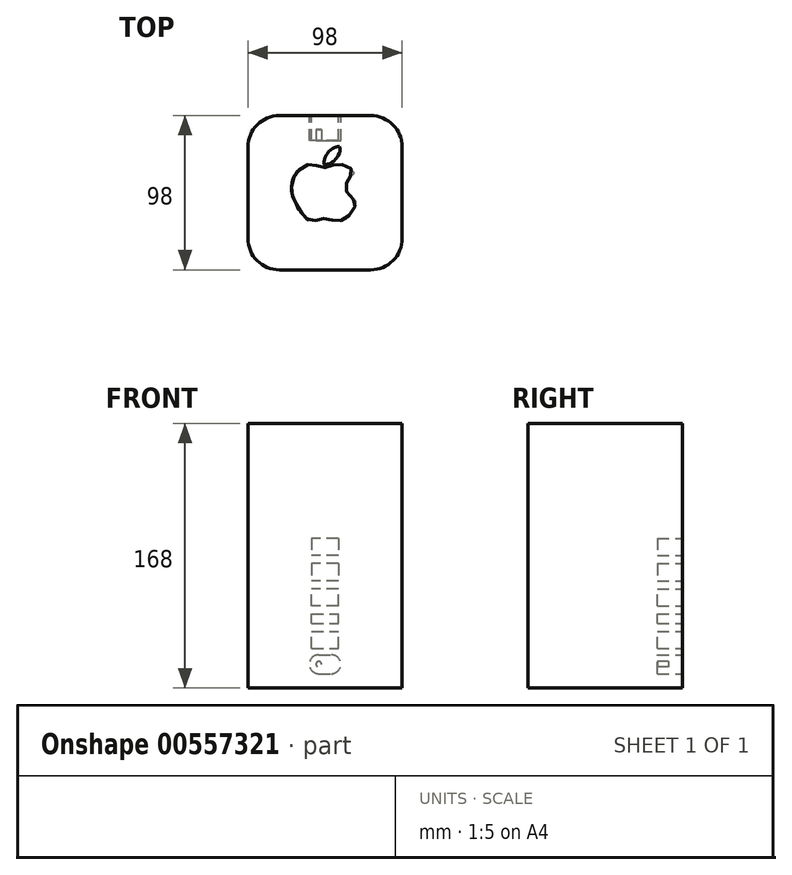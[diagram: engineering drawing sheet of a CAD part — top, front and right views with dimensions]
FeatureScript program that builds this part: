
annotation { "Feature Type Name" : "Feature", "Feature Type Description" : "" }
export const myFeature = defineFeature(function(context is Context, id is Id, definition is map)
    precondition{}
    {
        {
            var Q0;
            Q0=qCreatedBy(makeId("Top.planeOp"),FACE);
            var sketch = newSketch(context, id + "F0", { "sketchPlane" : qUnion([Q0])});
            skLineSegment(sketch, "E0.bottom", {"start": v(-49, 49) * mm, "end": v(49, 49) * mm});
            skLineSegment(sketch, "E0.top", {"start": v(-49, -49) * mm, "end": v(49, -49) * mm});
            skLineSegment(sketch, "E0.left", {"start": v(-49, 49) * mm, "end": v(-49, -49) * mm});
            skLineSegment(sketch, "E0.right", {"start": v(49, 49) * mm, "end": v(49, -49) * mm});
            skPoint(sketch, "E0.middle", {"position": v(0, 0) * mm});
            skSolve(sketch);
        }
        {
            var Q0;
            Q0=makeQuery(id+"F0.imprint","IMPRINT",FACE,{"disambiguationData":[TD([[makeQuery(id+"F0.imprint","IMPRINT",EDGE,{"derivedFrom":sQuery(id+"F0.wireOp",EDGE,"E0.bottom")}),-1.0]])]});
            extrude(context, id + "F1", {"entities" : qUnion([Q0]), "depth" : 168 * mm, "offsetDistance" : 25 * mm});
        }
        {
            var Q0;
            Q0=makeQuery(id+"F1.opExtrude","SWEPT_EDGE",EDGE,{"disambiguationData":[OSD([sQuery(id+"F0.wireOp",EDGE,"E0.top"),sQuery(id+"F0.wireOp",EDGE,"E0.left")])]});
            var Q1;
            Q1=makeQuery(id+"F1.opExtrude","SWEPT_EDGE",EDGE,{"disambiguationData":[OSD([sQuery(id+"F0.wireOp",EDGE,"E0.top"),sQuery(id+"F0.wireOp",EDGE,"E0.right")])]});
            var Q2;
            Q2=makeQuery(id+"F1.opExtrude","SWEPT_EDGE",EDGE,{"disambiguationData":[OSD([sQuery(id+"F0.wireOp",EDGE,"E0.bottom"),sQuery(id+"F0.wireOp",EDGE,"E0.right")])]});
            var Q3;
            Q3=makeQuery(id+"F1.opExtrude","SWEPT_EDGE",EDGE,{"disambiguationData":[OSD([sQuery(id+"F0.wireOp",EDGE,"E0.bottom"),sQuery(id+"F0.wireOp",EDGE,"E0.left")])]});
            fillet(context, id + "F2", {"entities" : qUnion([Q0, Q1, Q2, Q3]), "radius" : 20 * mm, "tangentPropagation" : true, "allowEdgeOverflow" : false});
        }
        {
            var Q0;
            Q0=makeQuery(id+"F1.opExtrude","CAP_FACE",FACE,{"disambiguationData":[OSD([sQuery(id+"F0.wireOp",EDGE,"E0.bottom"),sQuery(id+"F0.wireOp",EDGE,"E0.top"),sQuery(id+"F0.wireOp",EDGE,"E0.left"),sQuery(id+"F0.wireOp",EDGE,"E0.right")])],"isStart":false});
            var sketch = newSketch(context, id + "F3", { "sketchPlane" : qUnion([Q0])});
            skFitSpline(sketch, "E1", {"points": [v(-16.69, 14.53) * mm, v(-12.99, 17.2) * mm, v(-10.1, 17.82) * mm, v(-7.84, 17.82) * mm, v(-5.37, 17.4) * mm, v(-2.23, 16.17) * mm, v(-0.02, 15.97) * mm, v(2.03, 16.17) * mm, v(4.3, 17.4) * mm, v(7.18, 18.23) * mm, v(9.44, 18.02) * mm, v(12.73, 17.4) * mm, v(15.61, 15.97) * mm, v(18.5, 12.57) * mm, v(16.64, 11.03) * mm, v(15, 9.18) * mm, v(13.97, 6.91) * mm, v(13.35, 4.24) * mm, v(13.35, 1.77) * mm, v(14.38, -0.5) * mm, v(16.44, -3.17) * mm, v(19.73, -5.64) * mm, v(19.52, -7.5) * mm, v(18.29, -10.37) * mm, v(16.03, -13.66) * mm, v(12.73, -17.16) * mm, v(10.47, -17.78) * mm, v(8.41, -17.78) * mm, v(5.53, -17.37) * mm, v(2.65, -16.75) * mm, v(0.39, -16.34) * mm, v(-2.23, -16.54) * mm, v(-4.34, -17.57) * mm, v(-6.6, -17.57) * mm, v(-9.08, -17.57) * mm, v(-11.75, -16.34) * mm, v(-13.6, -14.49) * mm, v(-15.04, -12.63) * mm, v(-16.9, -10.17) * mm, v(-18.34, -7.28) * mm, v(-19.57, -4.82) * mm, v(-20.6, -1.73) * mm, v(-21.22, 1.15) * mm, v(-21.22, 3.42) * mm, v(-20.8, 6.91) * mm, v(-19.57, 10.41) * mm, v(-18.34, 12.57) * mm, v(-16.69, 14.53) * mm]});
            skFitSpline(sketch, "E2", {"points": [v(9.25, 29.4) * mm, v(9.53, 28.4) * mm, v(9.53, 27.2) * mm, v(9.25, 25.9) * mm, v(8.85, 24.61) * mm, v(8.18, 23.49) * mm, v(7.44, 22.42) * mm, v(6.77, 21.46) * mm, v(5.86, 20.56) * mm, v(5.02, 19.82) * mm, v(4.23, 19.26) * mm, v(2.7, 18.53) * mm, v(1.13, 18.07) * mm, v(0.11, 18.02) * mm, v(-0.62, 18.02) * mm, v(-0.67, 18.58) * mm, v(-0.67, 19.54) * mm, v(-0.5, 20.67) * mm, v(-0.22, 21.74) * mm, v(0.17, 22.8) * mm, v(0.68, 23.88) * mm, v(1.3, 24.67) * mm, v(2.09, 25.74) * mm, v(2.93, 26.7) * mm, v(4.17, 27.54) * mm, v(5.13, 28.22) * mm, v(6.65, 28.95) * mm, v(8.4, 29.4) * mm, v(9.25, 29.4) * mm]});
            skSolve(sketch);
        }
        {
            var Q0;
            Q0 = qSketchRegion(id + "F3", true);
            extrude(context, id + "F4", {"entities" : qUnion([Q0]), "operationType" : NewBodyOperationType.REMOVE, "oppositeDirection" : true, "depth" : 0.1 * mm, "offsetDistance" : 25 * mm});
        }
        {
            var Q0;
            Q0=makeQuery(id+"F1.opExtrude","SWEPT_FACE",FACE,{"disambiguationData":[OSD([sQuery(id+"F0.wireOp",EDGE,"E0.bottom")])]});
            var sketch = newSketch(context, id + "F5", { "sketchPlane" : qUnion([Q0])});
            skArc(sketch, "E3", {"start": v(4, 9) * mm, "mid": v(10, 15) * mm, "end": v(4, 21) * mm});
            skArc(sketch, "E4", {"start": v(-4, 21) * mm, "mid": v(-10, 15) * mm, "end": v(-4, 9) * mm});
            skLineSegment(sketch, "E5.bottom", {"start": v(8.5, 25) * mm, "end": v(-8.5, 25) * mm});
            skLineSegment(sketch, "E5.top", {"start": v(8.5, 36) * mm, "end": v(-8.5, 36) * mm});
            skLineSegment(sketch, "E5.left", {"start": v(8.5, 25) * mm, "end": v(8.5, 36) * mm});
            skLineSegment(sketch, "E5.right", {"start": v(-8.5, 25) * mm, "end": v(-8.5, 36) * mm});
            skLineSegment(sketch, "E6.bottom", {"start": v(8.5, 41) * mm, "end": v(-8.5, 41) * mm});
            skLineSegment(sketch, "E6.top", {"start": v(8.5, 47) * mm, "end": v(-8.5, 47) * mm});
            skLineSegment(sketch, "E6.left", {"start": v(8.5, 41) * mm, "end": v(8.5, 47) * mm});
            skLineSegment(sketch, "E6.right", {"start": v(-8.5, 41) * mm, "end": v(-8.5, 47) * mm});
            skLineSegment(sketch, "E7", {"start": v(4, 9) * mm, "end": v(-4, 9) * mm});
            skLineSegment(sketch, "E8", {"start": v(4, 21) * mm, "end": v(-4, 21) * mm});
            skLineSegment(sketch, "E9.bottom", {"start": v(-8.5, 52) * mm, "end": v(8.5, 52) * mm});
            skLineSegment(sketch, "E9.top", {"start": v(-8.5, 63) * mm, "end": v(8.5, 63) * mm});
            skLineSegment(sketch, "E9.left", {"start": v(-8.5, 52) * mm, "end": v(-8.5, 63) * mm});
            skLineSegment(sketch, "E9.right", {"start": v(8.5, 52) * mm, "end": v(8.5, 63) * mm});
            skLineSegment(sketch, "E10", {"start": v(-8.5, 44) * mm, "end": v(8.5, 44) * mm, "construction": true});
            skLineSegment(sketch, "E11.bottom", {"start": v(-8.5, 79) * mm, "end": v(8.5, 79) * mm});
            skLineSegment(sketch, "E11.top", {"start": v(-8.5, 68) * mm, "end": v(8.5, 68) * mm});
            skLineSegment(sketch, "E11.left", {"start": v(-8.5, 79) * mm, "end": v(-8.5, 68) * mm});
            skLineSegment(sketch, "E11.right", {"start": v(8.5, 79) * mm, "end": v(8.5, 68) * mm});
            skLineSegment(sketch, "E12.bottom", {"start": v(-8.5, 95) * mm, "end": v(8.5, 95) * mm});
            skLineSegment(sketch, "E12.top", {"start": v(-8.5, 84) * mm, "end": v(8.5, 84) * mm});
            skLineSegment(sketch, "E12.left", {"start": v(-8.5, 95) * mm, "end": v(-8.5, 84) * mm});
            skLineSegment(sketch, "E12.right", {"start": v(8.5, 95) * mm, "end": v(8.5, 84) * mm});
            skLineSegment(sketch, "E13", {"start": v(0, 79) * mm, "end": v(0, 84) * mm, "construction": true});
            skLineSegment(sketch, "E14", {"start": v(0, 63) * mm, "end": v(0, 68) * mm, "construction": true});
            skLineSegment(sketch, "E15", {"start": v(0, 36) * mm, "end": v(0, 41) * mm, "construction": true});
            skLineSegment(sketch, "E16", {"start": v(0, 47) * mm, "end": v(0, 52) * mm, "construction": true});
            skSolve(sketch);
        }
        {
            var Q0;
            Q0 = qSketchRegion(id + "F5", true);
            extrude(context, id + "F6", {"entities" : qUnion([Q0]), "operationType" : NewBodyOperationType.REMOVE, "oppositeDirection" : true, "depth" : 16 * mm, "offsetDistance" : 25 * mm});
        }
        {
            var Q0;
            Q0=makeQuery(id+"F6.boolean.opBoolean","COPY",FACE,{"derivedFrom":makeQuery(id+"F6.opExtrude","CAP_FACE",FACE,{"disambiguationData":[OSD([sQuery(id+"F5.wireOp",EDGE,"E3"),sQuery(id+"F5.wireOp",EDGE,"E4"),sQuery(id+"F5.wireOp",EDGE,"E7"),sQuery(id+"F5.wireOp",EDGE,"E8")])],"isStart":false})});
            var sketch = newSketch(context, id + "F7", { "sketchPlane" : qUnion([Q0])});
            skCircle(sketch, "E17", {"center": v(4, 15) * mm, "radius": 1.75 * mm});
            skSolve(sketch);
        }
        {
            var Q0;
            Q0 = qSketchRegion(id + "F7", true);
            var Q1;
            Q1=sQuery(id+"F7.wireOp",EDGE,"E17");
            extrude(context, id + "F8", {"entities" : qUnion([Q0]), "operationType" : NewBodyOperationType.ADD, "surfaceEntities" : qUnion([Q1]), "depth" : 7 * mm, "offsetDistance" : 25 * mm});
        }
    });
